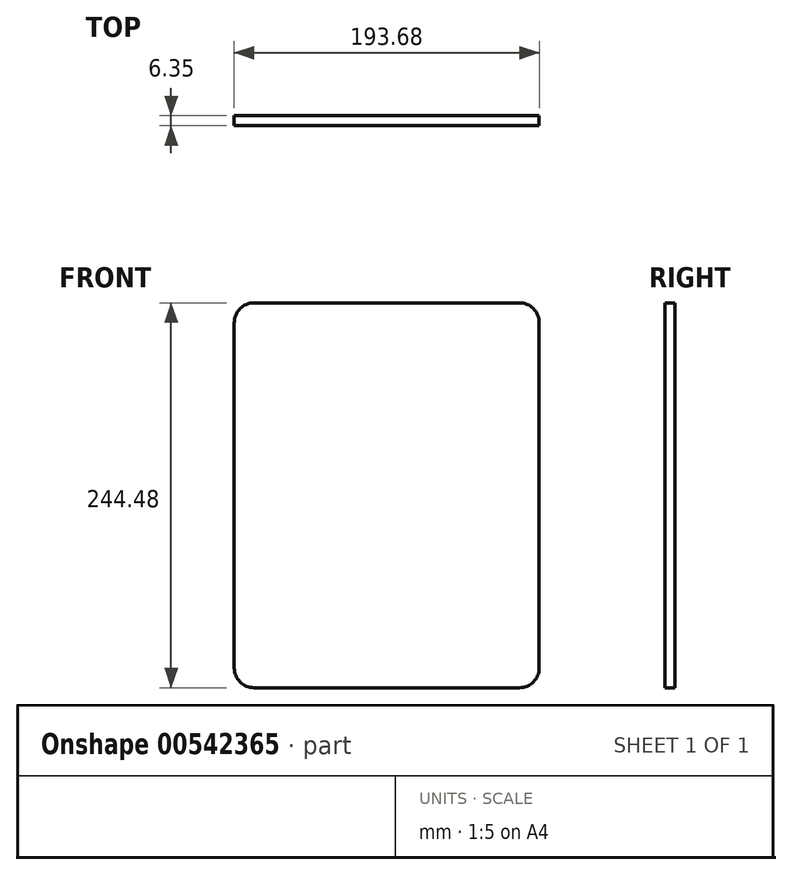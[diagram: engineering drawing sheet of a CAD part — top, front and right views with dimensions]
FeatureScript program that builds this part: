
annotation { "Feature Type Name" : "Feature", "Feature Type Description" : "" }
export const myFeature = defineFeature(function(context is Context, id is Id, definition is map)
    precondition{}
    {
        {
            var Q0;
            Q0=qCreatedBy(makeId("Front.planeOp"),FACE);
            var sketch = newSketch(context, id + "F0", { "sketchPlane" : qUnion([Q0])});
            skLineSegment(sketch, "E0.bottom", {"start": v(84.14, -122.24) * mm, "end": v(-84.14, -122.24) * mm});
            skLineSegment(sketch, "E0.top", {"start": v(84.14, 122.24) * mm, "end": v(-84.14, 122.24) * mm});
            skLineSegment(sketch, "E0.left", {"start": v(96.84, -109.54) * mm, "end": v(96.84, 109.54) * mm});
            skLineSegment(sketch, "E0.right", {"start": v(-96.84, -109.54) * mm, "end": v(-96.84, 109.54) * mm});
            skPoint(sketch, "E0.middle", {"position": v(0, 0) * mm});
            skPoint(sketch, "E1.visualSharp", {"position": v(-96.84, 122.24) * mm});
            skArc(sketch, "E1.filletArc", {"start": v(-84.14, 122.24) * mm, "mid": v(-93.12, 118.52) * mm, "end": v(-96.84, 109.54) * mm});
            skPoint(sketch, "E2.visualSharp", {"position": v(96.84, 122.24) * mm});
            skArc(sketch, "E2.filletArc", {"start": v(96.84, 109.54) * mm, "mid": v(93.12, 118.52) * mm, "end": v(84.14, 122.24) * mm});
            skPoint(sketch, "E3.visualSharp", {"position": v(96.84, -122.24) * mm});
            skArc(sketch, "E3.filletArc", {"start": v(84.14, -122.24) * mm, "mid": v(93.12, -118.52) * mm, "end": v(96.84, -109.54) * mm});
            skPoint(sketch, "E4.visualSharp", {"position": v(-96.84, -122.24) * mm});
            skArc(sketch, "E4.filletArc", {"start": v(-96.84, -109.54) * mm, "mid": v(-93.12, -118.52) * mm, "end": v(-84.14, -122.24) * mm});
            skSolve(sketch);
        }
        {
            var Q0;
            Q0=makeQuery(id+"F0.imprint","IMPRINT",FACE,{"disambiguationData":[TD([[makeQuery(id+"F0.imprint","IMPRINT",EDGE,{"derivedFrom":sQuery(id+"F0.wireOp",EDGE,"E0.bottom")}),-1.0]])]});
            extrude(context, id + "F1", {"entities" : qUnion([Q0]), "depth" : 6.35 * mm, "offsetDistance" : 25.4 * mm});
        }
    });
